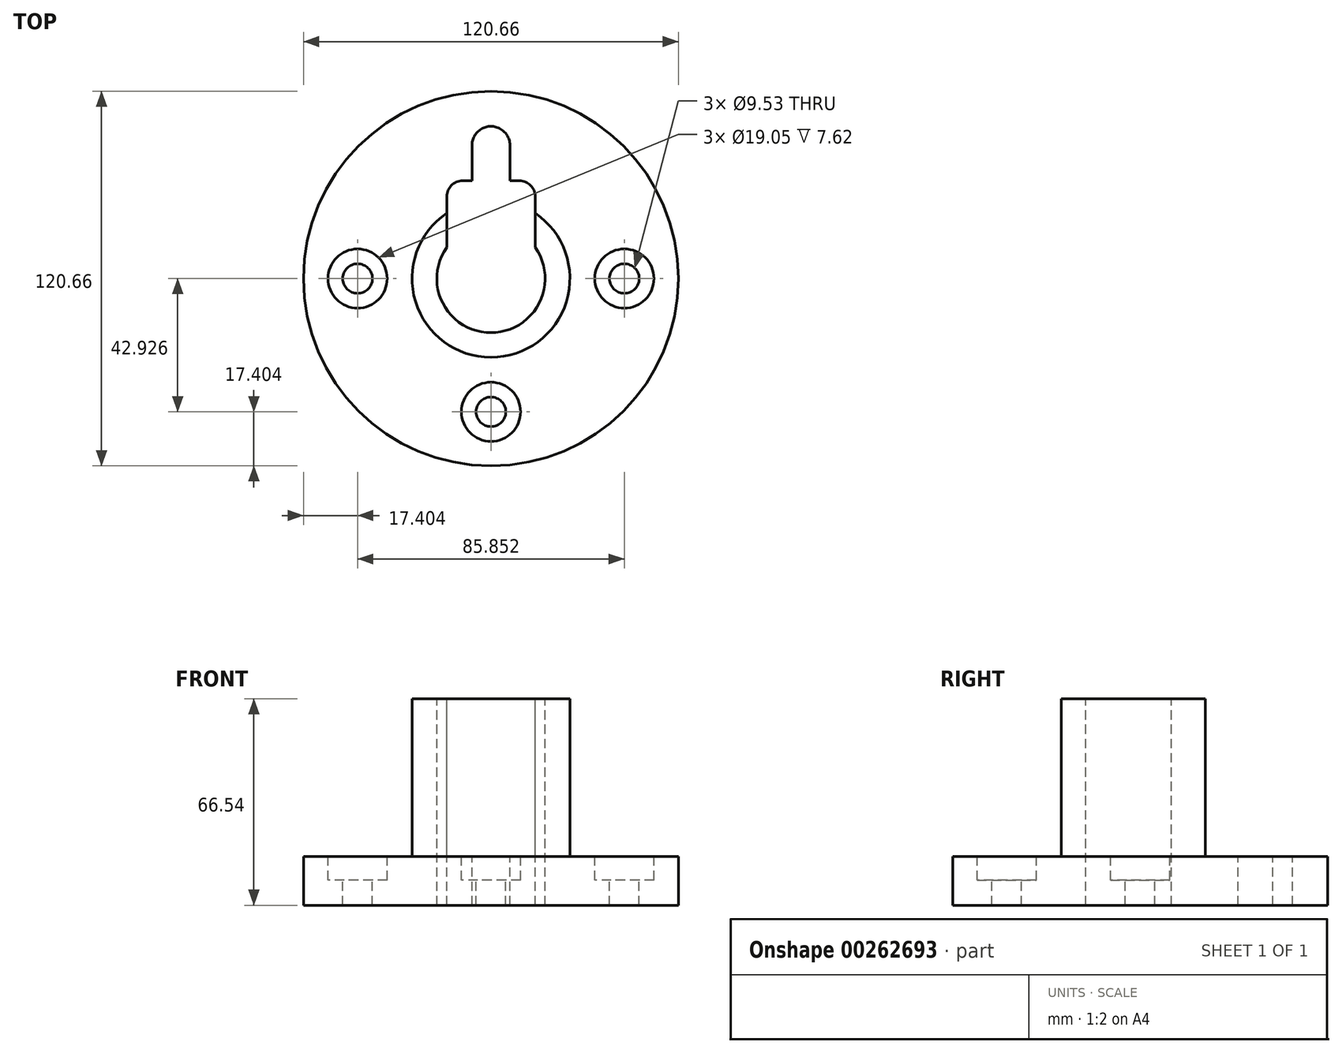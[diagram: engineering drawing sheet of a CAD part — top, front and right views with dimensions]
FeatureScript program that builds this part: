
annotation { "Feature Type Name" : "Feature", "Feature Type Description" : "" }
export const myFeature = defineFeature(function(context is Context, id is Id, definition is map)
    precondition{}
    {
        {
            var Q0;
            Q0=qCreatedBy(makeId("Front.planeOp"),FACE);
            var sketch = newSketch(context, id + "F0", { "sketchPlane" : qUnion([Q0])});
            skLineSegment(sketch, "E0.bottom", {"start": v(25.4, 27.9) * mm, "end": v(0, 27.9) * mm});
            skLineSegment(sketch, "E0.top", {"start": v(25.4, -38.65) * mm, "end": v(-34.92, -38.65) * mm});
            skLineSegment(sketch, "E0.left", {"start": v(25.4, 27.9) * mm, "end": v(25.4, -38.65) * mm});
            skLineSegment(sketch, "E0.right", {"start": v(-34.92, -22.9) * mm, "end": v(-34.92, -38.65) * mm});
            skLineSegment(sketch, "E1", {"start": v(0, 27.9) * mm, "end": v(0, -22.9) * mm});
            skLineSegment(sketch, "E2", {"start": v(0, -22.9) * mm, "end": v(-34.92, -22.9) * mm});
            skSolve(sketch);
        }
        {
            var Q0;
            Q0 = qSketchRegion(id + "F0", true);
            var Q1;
            Q1=sQuery(id+"F0.wireOp",EDGE,"E0.left");
            revolve(context, id + "F1", {"entities" : qUnion([Q0]), "axis" : qUnion([Q1]), "revolveType" : RevolveType.FULL});
        }
        {
            var Q0;
            Q0=makeQuery(id+"F1.opRevolve","SWEPT_FACE",FACE,{"disambiguationData":[OSD([sQuery(id+"F0.wireOp",EDGE,"E0.bottom")])]});
            var sketch = newSketch(context, id + "F2", { "sketchPlane" : qUnion([Q0])});
            skCircle(sketch, "E3", {"center": v(25.4, 0) * mm, "radius": 17.42 * mm});
            skSolve(sketch);
        }
        {
            var Q0;
            Q0 = qSketchRegion(id + "F2", true);
            extrude(context, id + "F3", {"entities" : qUnion([Q0]), "operationType" : NewBodyOperationType.REMOVE, "oppositeDirection" : true, "depth" : 101.6 * mm});
        }
        {
            var Q0;
            Q0=makeQuery(id+"F1.opRevolve","SWEPT_FACE",FACE,{"disambiguationData":[OSD([sQuery(id+"F0.wireOp",EDGE,"E2")])]});
            var sketch = newSketch(context, id + "F4", { "sketchPlane" : qUnion([Q0])});
            skCircle(sketch, "E4", {"center": v(68.33, 0) * mm, "radius": 9.53 * mm});
            skCircle(sketch, "E5.1.0", {"center": v(25.4, -42.93) * mm, "radius": 9.53 * mm});
            skCircle(sketch, "E5.2.0", {"center": v(-17.53, 0) * mm, "radius": 9.53 * mm});
            skPoint(sketch, "E5.center", {"position": v(25.4, 0) * mm});
            skSolve(sketch);
        }
        {
            var Q0;
            Q0=sQuery(id+"F4.wireOp",VERTEX,"E5.2.0.center");
            var Q1;
            Q1=sQuery(id+"F4.wireOp",VERTEX,"E5.1.0.center");
            var Q2;
            Q2=sQuery(id+"F4.wireOp",VERTEX,"E4.center");
            var Q3;
            Q3=makeQuery(id+"F1.opRevolve","SWEPT_BODY",BODY,{"disambiguationData":[OSD([sQuery(id+"F0.wireOp",EDGE,"E0.bottom"),sQuery(id+"F0.wireOp",EDGE,"E0.top"),sQuery(id+"F0.wireOp",EDGE,"E0.left"),sQuery(id+"F0.wireOp",EDGE,"E0.right"),sQuery(id+"F0.wireOp",EDGE,"E1"),sQuery(id+"F0.wireOp",EDGE,"E2")])]});
            hole(context, id + "F5", {"style" : HoleStyle.C_BORE, "endStyle" : HoleEndStyle.THROUGH, "holeDiameter" : 9.52 * mm, "cBoreDiameter" : 19.05 * mm, "cBoreDepth" : 7.62 * mm, "tappedDepth" : 12.7 * mm, "tapClearance" : 3, "startFromSketch" : true, "locations" : qUnion([Q0, Q1, Q2]), "scope" : qUnion([Q3])});
        }
        {
            var Q0;
            Q0=makeQuery(id+"F1.opRevolve","SWEPT_FACE",FACE,{"disambiguationData":[OSD([sQuery(id+"F0.wireOp",EDGE,"E0.bottom")])]});
            var sketch = newSketch(context, id + "F6", { "sketchPlane" : qUnion([Q0])});
            skLineSegment(sketch, "E6.bottom", {"start": v(39.62, 0) * mm, "end": v(11.18, 0) * mm});
            skLineSegment(sketch, "E6.top", {"start": v(39.62, 31.5) * mm, "end": v(31.5, 31.5) * mm});
            skLineSegment(sketch, "E6.left", {"start": v(39.62, 0) * mm, "end": v(39.62, 31.5) * mm});
            skLineSegment(sketch, "E6.right", {"start": v(11.18, 0) * mm, "end": v(11.18, 31.5) * mm});
            skPoint(sketch, "E7.endSnap0", {"position": v(25.4, 31.5) * mm});
            skArc(sketch, "E8", {"start": v(31.5, 42.67) * mm, "mid": v(25.4, 49.02) * mm, "end": v(19.3, 42.67) * mm});
            skLineSegment(sketch, "E9", {"start": v(19.3, 42.67) * mm, "end": v(19.3, 31.5) * mm});
            skLineSegment(sketch, "E10", {"start": v(31.5, 42.67) * mm, "end": v(31.5, 31.5) * mm});
            skPoint(sketch, "E7.start.orphan", {"position": v(25.4, 0) * mm});
            skLineSegment(sketch, "E11.trimOffspring", {"start": v(19.3, 31.5) * mm, "end": v(11.18, 31.5) * mm});
            skSolve(sketch);
        }
        {
            var Q0;
            Q0 = qSketchRegion(id + "F6", true);
            extrude(context, id + "F7", {"entities" : qUnion([Q0]), "operationType" : NewBodyOperationType.REMOVE, "oppositeDirection" : true, "depth" : 838.2 * mm});
        }
        {
            var Q0;
            Q0=makeQuery(id+"F7.boolean.opBoolean","COPY",EDGE,{"derivedFrom":makeQuery(id+"F7.opExtrude","SWEPT_EDGE",EDGE,{"disambiguationData":[OSD([sQuery(id+"F6.wireOp",EDGE,"E6.right"),sQuery(id+"F6.wireOp",EDGE,"E11.trimOffspring")])]})});
            var Q1;
            Q1=makeQuery(id+"F7.boolean.opBoolean","COPY",EDGE,{"derivedFrom":makeQuery(id+"F7.opExtrude","SWEPT_EDGE",EDGE,{"disambiguationData":[OSD([sQuery(id+"F6.wireOp",EDGE,"E6.top"),sQuery(id+"F6.wireOp",EDGE,"E6.left")])]})});
            fillet(context, id + "F8", {"entities" : qUnion([Q0, Q1]), "radius" : 5.08 * mm, "tangentPropagation" : true, "allowEdgeOverflow" : false});
        }
    });
